# Revit family: Domotics-DomesticRanges-GEWISS-CHORUS_COMMAND-BLANKING_MODULE
name_source: partatom
category: Apparecchi elettrici
revit_build: Autodesk Revit 2016 (Build: 20161004_0715(x64)
units: mm (PartAtom-declared; Revit-internal decimal feet)

## family parameters
Condiviso = Sì
Host = Superficie
Mantenere orientamento annotazione = Sì
Punto di calcolo locali = Sì
Quota connettore circolare = Usa diametro
Taglio con vuoti quando caricato = Sì
Tipo di parte = Normale

## types (12) — shared parameters
Altezza_copriforo = 45 mm  [stored 0.147638 ft]
Bidimensionale = bidimensionale copriforo bidimensionale : Simbolo bidimensionle
Catalogue = DOMOTICS
Catalogue Range = CHORUS - DOMESTIC RANGE
Category = Blanking module
Electrocod = 0100
Glow Wire Test = 850°C
IDF = 26b059a0-c2c7-400f-ae45-4f618bb426d1
IDT = aa89deda-6b8d-4a04-ba6c-0083ea0ab4c4
Larghezza copriforo = 69 mm  [stored 0.226378 ft]
Produttore = GEWISS S.p.A.
Prospetto di default = 1219 mm
SEO = Blanking module
Standard = EN 60669-1
Standard; = EN 60669-1
Technical sheet = https://www.gewiss.com
Thermo-pressure with ball = 125
Tipo_ = CHORUS COPRIFORO_generico : GW14199 Copriforo 3M titanio
URL = https://www.gewiss.com
Version file RFA = 19.0

## per-type parameters (varying)
| type | Colour | Description: | Descrizione | EAN code | Modello | No. Chorus modules |
| GW10197 - Blanking module 1/2M white | White | 1/2 gang | BLANKING MODULE 1/2M WHITE | 8011564260658 | GW10197 | 1/2 |
| GW12197 - Blanking module 1/2M black | Black | 1/2 gang | BLANKING MODULE, 1/2M, BLACK | 8011564266827 | GW12197 | 1/2 |
| GW12195 - Blanking module 1M black | Black | 1 gang | BLANKING MODULE, 1M, BLACK | 8011564269668 | GW12195 | 1 |
| GW14197 - Blanking module 1/2M titanium | Titanium | 1/2 gang | BLANKING MODULE, 1/2M, TITANIUM | 8011564266261 | GW14197 | 1/2 |
| GW10195 - Blanking module 1M white | White | 1 gang | BLANKING MODULE 1M WHITE | 8011564262287 | GW10195 | 1 |
| GW10198 - Blanking module 2M white | White | 2 gang | BLANKING MODULE 2M WHITE | 8011564258952 | GW10198 | 2 |
| GW10199 - Blanking module 3M white | White | 3 gang | BLANKING MODULE 3M WHITE | 8011564259027 | GW10199 | 3 |
| GW14199 - Blanking module 3M titanium | Titanium | 3 gang | BLANKING MODULE, 3M, TITANIUM | 8011564266285 | GW14199 | 3 |
| GW14195 - Blanking module 1M titanium | Titanium | 1 gang | BLANKING MODULE, 1M, TITANIUM | 8011564266247 | GW14195 | 1 |
| GW14198 - Blanking module 2M titanium | Titanium | 2 gang | BLANKING MODULE, 2M, TITANIUM | 8011564266278 | GW14198 | 2 |
| GW12199 - Blanking module 3M black | Black | 3 gang | BLANKING MODULE, 3M, BLACK | 8011564266650 | GW12199 | 3 |
| GW12198 - Blanking module 2M black | Black | 2 gang | BLANKING MODULE, 2M, BLACK | 8011564266643 | GW12198 | 2 |

note: source unit labels omitted for Thermo-pressure with ball — the stored unit's dimension contradicts the parameter name (converter mislabeling)

note: [stored X ft] marks values corroborated as IEEE doubles in the binary element streams (Revit-internal decimal feet)

## geometry (parser evidence)
native form markers: Sweep x6
no freeform markers — native parametric forms only
